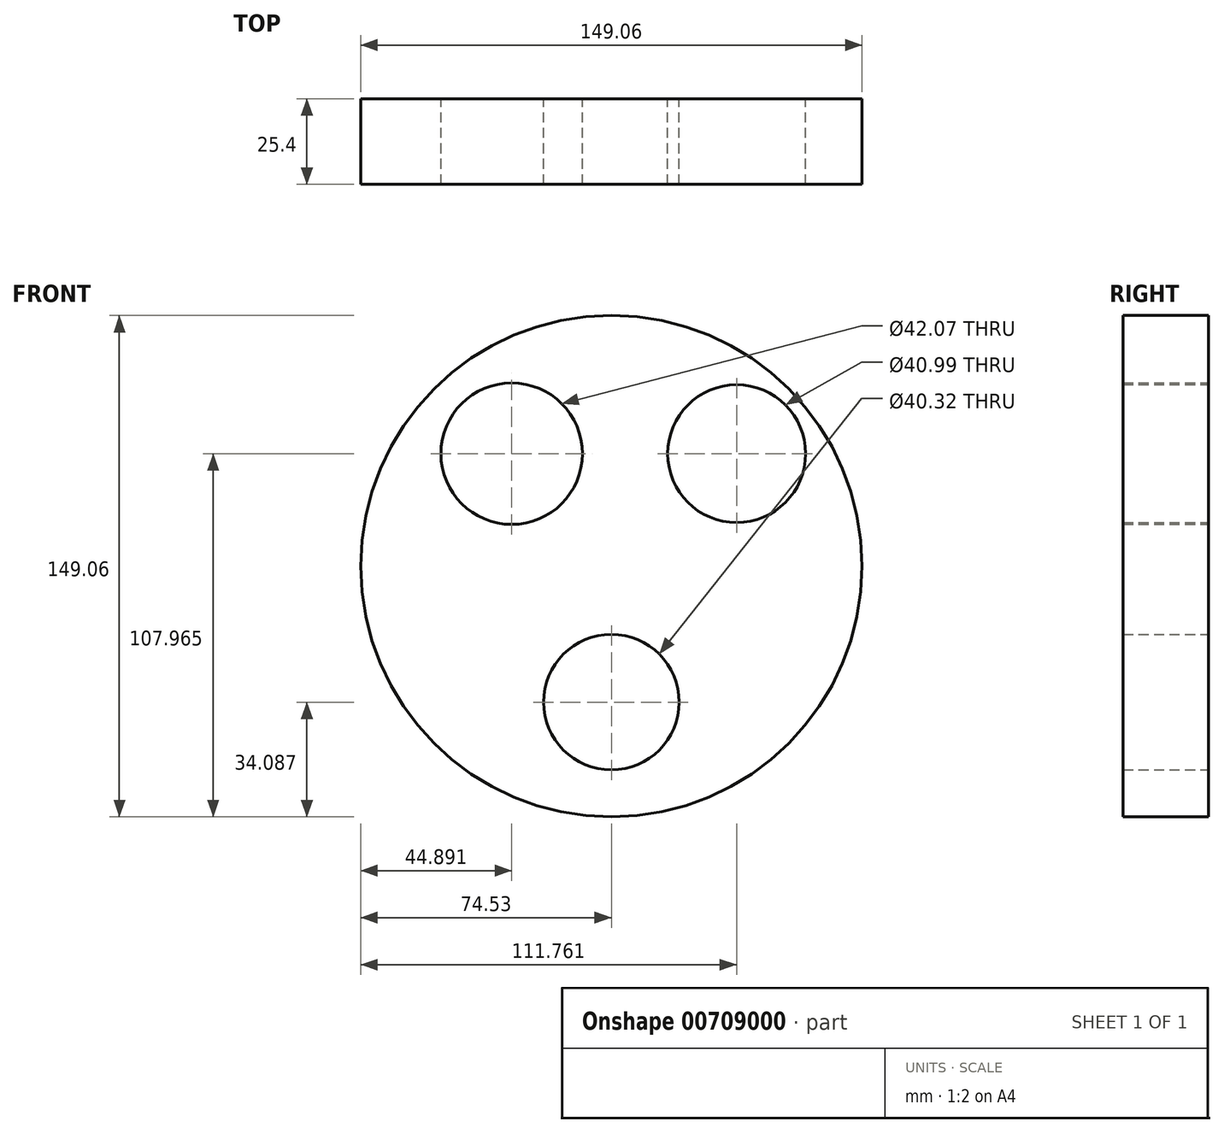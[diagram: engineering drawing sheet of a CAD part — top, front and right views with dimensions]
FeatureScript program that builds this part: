
annotation { "Feature Type Name" : "Feature", "Feature Type Description" : "" }
export const myFeature = defineFeature(function(context is Context, id is Id, definition is map)
    precondition{}
    {
        {
            var Q0;
            Q0=qCreatedBy(makeId("Front.planeOp"),FACE);
            var sketch = newSketch(context, id + "F0", { "sketchPlane" : qUnion([Q0])});
            skCircle(sketch, "E0", {"center": v(0, 0) * mm, "radius": 74.53 * mm});
            skCircle(sketch, "E1", {"center": v(-29.64, 33.43) * mm, "radius": 21.03 * mm});
            skCircle(sketch, "E2", {"center": v(37.23, 33.43) * mm, "radius": 20.5 * mm});
            skCircle(sketch, "E3", {"center": v(0, -40.44) * mm, "radius": 20.16 * mm});
            skSolve(sketch);
        }
        {
            var Q0;
            Q0 = qSketchRegion(id + "F0", true);
            extrude(context, id + "F1", {"entities" : qUnion([Q0]), "depth" : 25.4 * mm, "offsetDistance" : 25.4 * mm});
        }
    });
